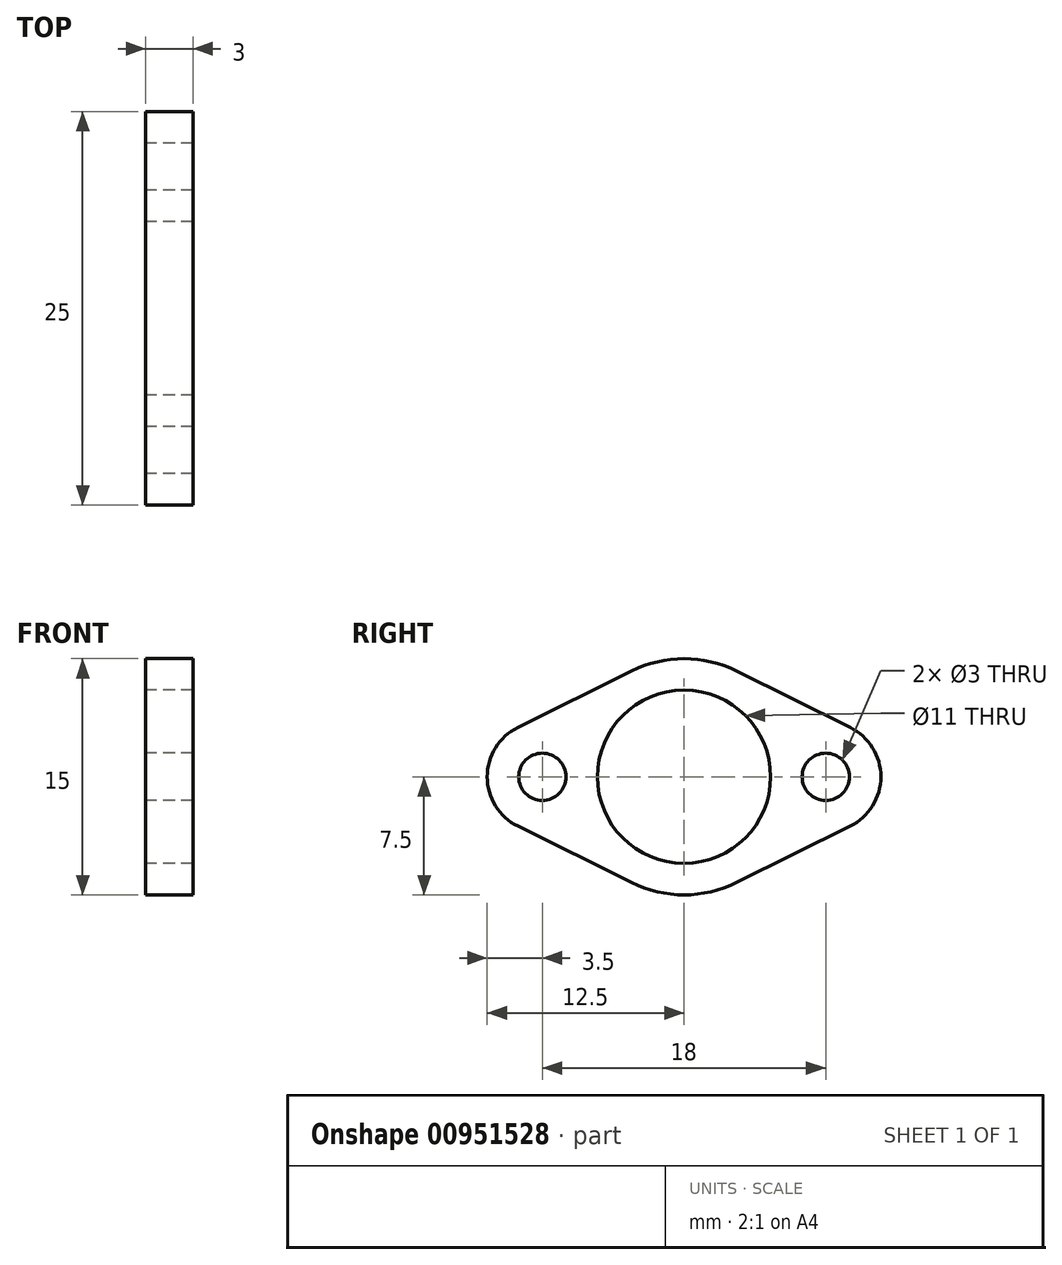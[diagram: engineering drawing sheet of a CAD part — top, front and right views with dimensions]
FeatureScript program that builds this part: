
annotation { "Feature Type Name" : "Feature", "Feature Type Description" : "" }
export const myFeature = defineFeature(function(context is Context, id is Id, definition is map)
    precondition{}
    {
        {
            var Q0;
            Q0=qCreatedBy(makeId("Right.planeOp"),FACE);
            var sketch = newSketch(context, id + "F0", { "sketchPlane" : qUnion([Q0])});
            skCircle(sketch, "E0", {"center": v(0, 0) * mm, "radius": 5.5 * mm});
            skCircle(sketch, "E1", {"center": v(9, 0) * mm, "radius": 3.5 * mm});
            skCircle(sketch, "E2", {"center": v(-9, 0) * mm, "radius": 1.5 * mm});
            skCircle(sketch, "E3", {"center": v(0, 0) * mm, "radius": 7.5 * mm});
            skCircle(sketch, "E4", {"center": v(-9, 0) * mm, "radius": 3.5 * mm});
            skCircle(sketch, "E5", {"center": v(9, 0) * mm, "radius": 1.5 * mm});
            skLineSegment(sketch, "E6", {"start": v(-10.56, 3.14) * mm, "end": v(-3.33, 6.72) * mm});
            skLineSegment(sketch, "E7", {"start": v(3.33, 6.72) * mm, "end": v(10.56, 3.14) * mm});
            skLineSegment(sketch, "E8", {"start": v(10.56, -3.14) * mm, "end": v(3.33, -6.72) * mm});
            skLineSegment(sketch, "E9", {"start": v(-10.56, -3.14) * mm, "end": v(-3.33, -6.72) * mm});
            skSolve(sketch);
        }
        {
            var Q0;
            {var subQ4=sQuery(id+"F0.wireOp",EDGE,"E2");Q0=makeQuery(id+"F0.imprint","IMPRINT",FACE,{"disambiguationData":[TD([[makeQuery(id+"F0.imprint","IMPRINT",EDGE,{"derivedFrom":subQ4}),-1.0]])]});}
            var Q1;
            {var subQ0=sQuery(id+"F0.wireOp",EDGE,"E3");var subQ1=makeQuery(id+"F0.imprint","INTERSECT",VERTEX,{"derivedFrom":[sQuery(id+"F0.wireOp",EDGE,"E2"),subQ0]});Q1=makeQuery(id+"F0.imprint","IMPRINT",FACE,{"disambiguationData":[TD([[makeQuery(id+"F0.imprint","IMPRINT",EDGE,{"disambiguationData":[TD([[subQ1,1.0]])],"derivedFrom":subQ0}),1.0]])]});}
            var Q2;
            {var subQ0=sQuery(id+"F0.wireOp",EDGE,"E6");Q2=makeQuery(id+"F0.imprint","IMPRINT",FACE,{"disambiguationData":[TD([[makeQuery(id+"F0.imprint","IMPRINT",EDGE,{"derivedFrom":subQ0}),-1.0]])]});}
            var Q3;
            {var subQ2=sQuery(id+"F0.wireOp",EDGE,"E1");var subQ4=sQuery(id+"F0.wireOp",EDGE,"E0");var subQ5=makeQuery(id+"F0.imprint","INTERSECT",VERTEX,{"derivedFrom":[subQ4,subQ2]});Q3=makeQuery(id+"F0.imprint","IMPRINT",FACE,{"disambiguationData":[TD([[makeQuery(id+"F0.imprint","IMPRINT",EDGE,{"disambiguationData":[TD([[subQ5,-1.0]])],"derivedFrom":subQ4}),-1.0]])]});}
            var Q4;
            {var subQ0=sQuery(id+"F0.wireOp",EDGE,"E9");Q4=makeQuery(id+"F0.imprint","IMPRINT",FACE,{"disambiguationData":[TD([[makeQuery(id+"F0.imprint","IMPRINT",EDGE,{"derivedFrom":subQ0}),1.0]])]});}
            var Q5;
            {var subQ3=sQuery(id+"F0.wireOp",EDGE,"E1");var subQ4=sQuery(id+"F0.wireOp",EDGE,"E0");var subQ5=makeQuery(id+"F0.imprint","INTERSECT",VERTEX,{"derivedFrom":[subQ4,subQ3]});Q5=makeQuery(id+"F0.imprint","IMPRINT",FACE,{"disambiguationData":[TD([[makeQuery(id+"F0.imprint","IMPRINT",EDGE,{"disambiguationData":[TD([[subQ5,1.0]])],"derivedFrom":subQ4}),-1.0]])]});}
            var Q6;
            {var subQ0=sQuery(id+"F0.wireOp",EDGE,"E1");var subQ1=makeQuery(id+"F0.imprint","INTERSECT",VERTEX,{"derivedFrom":[sQuery(id+"F0.wireOp",EDGE,"E0"),subQ0]});Q6=makeQuery(id+"F0.imprint","IMPRINT",FACE,{"disambiguationData":[TD([[makeQuery(id+"F0.imprint","IMPRINT",EDGE,{"disambiguationData":[TD([[subQ1,1.0]])],"derivedFrom":subQ0}),1.0]])]});}
            var Q7;
            {var subQ0=sQuery(id+"F0.wireOp",EDGE,"E5");Q7=makeQuery(id+"F0.imprint","IMPRINT",FACE,{"disambiguationData":[TD([[makeQuery(id+"F0.imprint","IMPRINT",EDGE,{"derivedFrom":subQ0}),-1.0]])]});}
            var Q8;
            {var subQ0=sQuery(id+"F0.wireOp",EDGE,"E7");Q8=makeQuery(id+"F0.imprint","IMPRINT",FACE,{"disambiguationData":[TD([[makeQuery(id+"F0.imprint","IMPRINT",EDGE,{"derivedFrom":subQ0}),-1.0]])]});}
            var Q9;
            {var subQ0=sQuery(id+"F0.wireOp",EDGE,"E8");Q9=makeQuery(id+"F0.imprint","IMPRINT",FACE,{"disambiguationData":[TD([[makeQuery(id+"F0.imprint","IMPRINT",EDGE,{"derivedFrom":subQ0}),-1.0]])]});}
            extrude(context, id + "F1", {"entities" : qUnion([Q0, Q1, Q2, Q3, Q4, Q5, Q6, Q7, Q8, Q9]), "depth" : 3 * mm, "offsetDistance" : 25 * mm});
        }
    });
